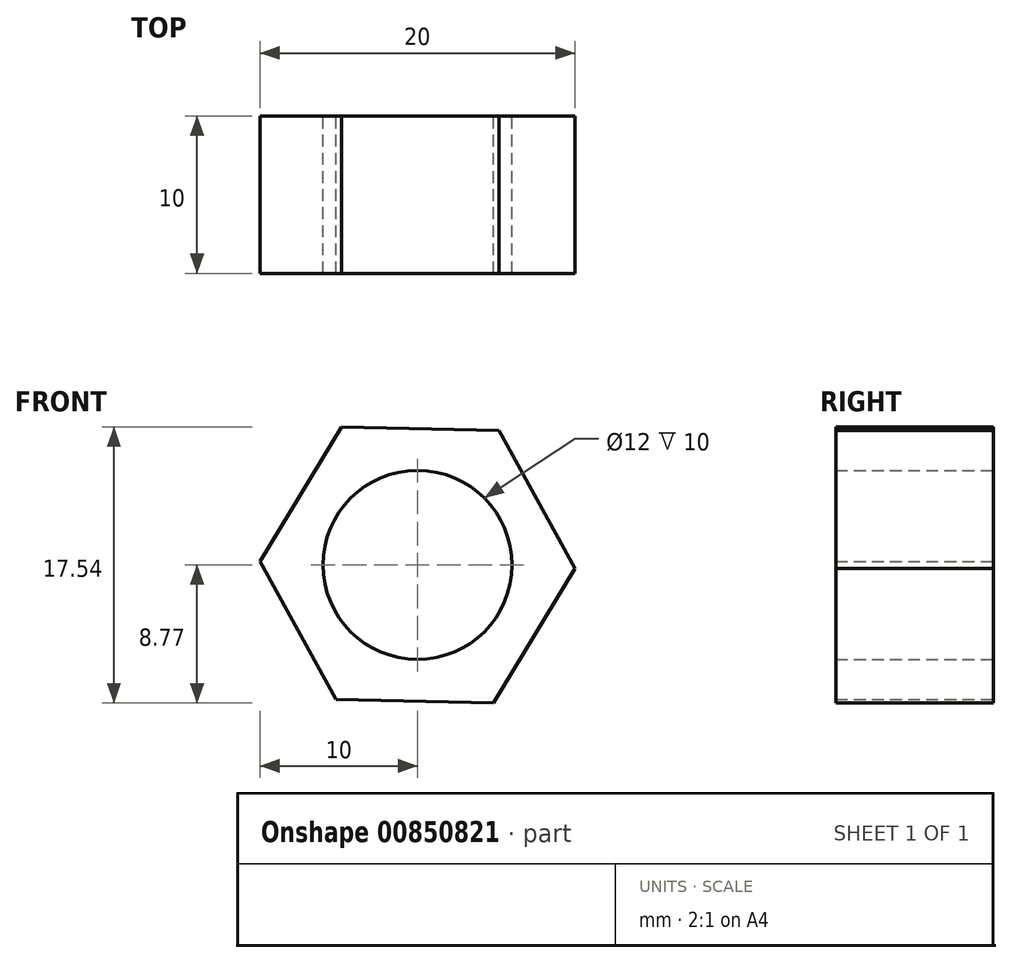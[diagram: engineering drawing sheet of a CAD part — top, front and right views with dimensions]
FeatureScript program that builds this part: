
annotation { "Feature Type Name" : "Feature", "Feature Type Description" : "" }
export const myFeature = defineFeature(function(context is Context, id is Id, definition is map)
    precondition{}
    {
        {
            var Q0;
            Q0=qCreatedBy(makeId("Front.planeOp"),FACE);
            var sketch = newSketch(context, id + "F0", { "sketchPlane" : qUnion([Q0])});
            skCircle(sketch, "E0.cCircle", {"center": v(0, 0) * mm, "radius": 8.66 * mm, "construction": true});
            skLineSegment(sketch, "E0.0", {"start": v(10, -0.21) * mm, "end": v(4.81, -8.77) * mm});
            skLineSegment(sketch, "E0.1", {"start": v(4.81, -8.77) * mm, "end": v(-5.18, -8.55) * mm});
            skLineSegment(sketch, "E0.2", {"start": v(-5.18, -8.55) * mm, "end": v(-10, 0.21) * mm});
            skLineSegment(sketch, "E0.3", {"start": v(-10, 0.21) * mm, "end": v(-4.81, 8.77) * mm});
            skLineSegment(sketch, "E0.4", {"start": v(-4.81, 8.77) * mm, "end": v(5.18, 8.55) * mm});
            skLineSegment(sketch, "E0.5", {"start": v(5.18, 8.55) * mm, "end": v(10, -0.21) * mm});
            skPoint(sketch, "E0.0.midPoint", {"position": v(7.4, -4.49) * mm});
            skCircle(sketch, "E1", {"center": v(0, 0) * mm, "radius": 6 * mm});
            skSolve(sketch);
        }
        {
            var Q0;
            Q0=qSketchRegion(id+"F0",true);
            extrude(context, id + "F1", {"entities" : qUnion([Q0]), "depth" : 10 * mm, "offsetDistance" : 25 * mm});
        }
    });
